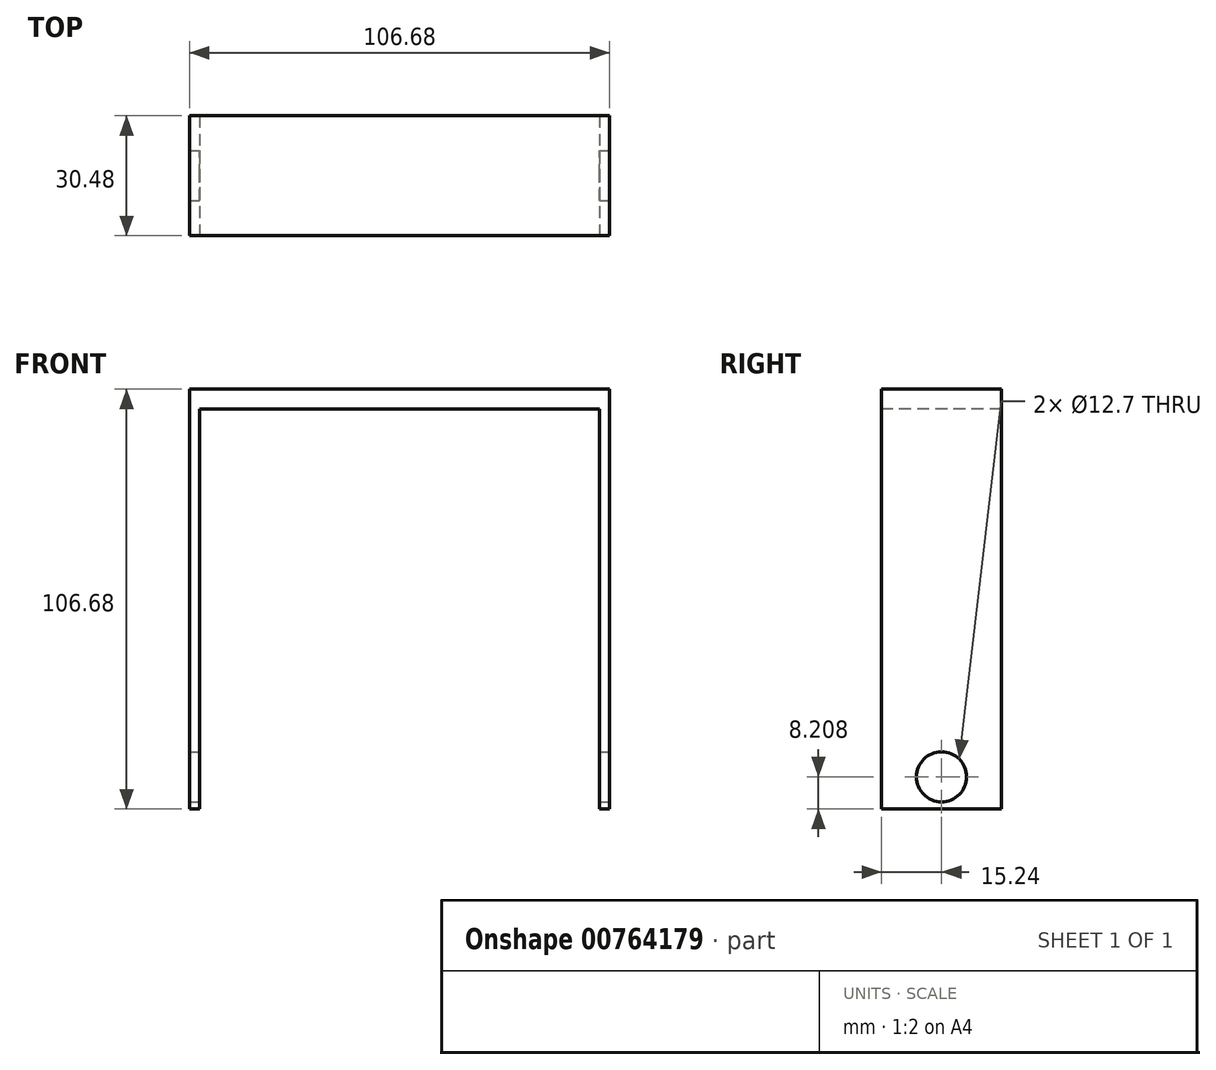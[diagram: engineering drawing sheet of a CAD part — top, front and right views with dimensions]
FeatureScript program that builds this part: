
annotation { "Feature Type Name" : "Feature", "Feature Type Description" : "" }
export const myFeature = defineFeature(function(context is Context, id is Id, definition is map)
    precondition{}
    {
        {
            var Q0;
            Q0=qCreatedBy(makeId("Front.planeOp"),FACE);
            var sketch = newSketch(context, id + "F0", { "sketchPlane" : qUnion([Q0])});
            skLineSegment(sketch, "E0.bottom", {"start": v(0, 0) * mm, "end": v(106.68, 0) * mm});
            skLineSegment(sketch, "E0.top", {"start": v(0, 106.68) * mm, "end": v(106.68, 106.68) * mm});
            skLineSegment(sketch, "E0.left", {"start": v(0, 0) * mm, "end": v(0, 106.68) * mm});
            skLineSegment(sketch, "E0.right", {"start": v(106.68, 0) * mm, "end": v(106.68, 106.68) * mm});
            skSolve(sketch);
        }
        {
            var Q0;
            Q0=makeQuery(id+"F0.imprint","IMPRINT",FACE,{"disambiguationData":[TD([[makeQuery(id+"F0.imprint","IMPRINT",EDGE,{"derivedFrom":sQuery(id+"F0.wireOp",EDGE,"E0.bottom")}),1.0]])]});
            extrude(context, id + "F1", {"entities" : qUnion([Q0]), "depth" : 30.48 * mm, "offsetDistance" : 25.4 * mm});
        }
        {
            var Q0;
            Q0=makeQuery(id+"F1.opExtrude","CAP_FACE",FACE,{"disambiguationData":[OSD([sQuery(id+"F0.wireOp",EDGE,"E0.bottom"),sQuery(id+"F0.wireOp",EDGE,"E0.top"),sQuery(id+"F0.wireOp",EDGE,"E0.left"),sQuery(id+"F0.wireOp",EDGE,"E0.right")])],"isStart":false});
            var sketch = newSketch(context, id + "F2", { "sketchPlane" : qUnion([Q0])});
            skLineSegment(sketch, "E1.bottom", {"start": v(2.54, 0) * mm, "end": v(104.14, 0) * mm});
            skLineSegment(sketch, "E1.top", {"start": v(2.54, 101.6) * mm, "end": v(104.14, 101.6) * mm});
            skLineSegment(sketch, "E1.left", {"start": v(2.54, 0) * mm, "end": v(2.54, 101.6) * mm});
            skLineSegment(sketch, "E1.right", {"start": v(104.14, 0) * mm, "end": v(104.14, 101.6) * mm});
            skSolve(sketch);
        }
        {
            var Q0;
            Q0=makeQuery(id+"F2.imprint","IMPRINT",FACE,{"disambiguationData":[TD([[makeQuery(id+"F2.imprint","IMPRINT",EDGE,{"derivedFrom":sQuery(id+"F2.wireOp",EDGE,"E1.bottom")}),1.0]])]});
            extrude(context, id + "F3", {"entities" : qUnion([Q0]), "operationType" : NewBodyOperationType.REMOVE, "oppositeDirection" : true, "depth" : 30.48 * mm, "offsetDistance" : 25.4 * mm});
        }
        {
            var Q0;
            Q0=makeQuery(id+"F1.opExtrude","SWEPT_FACE",FACE,{"disambiguationData":[OSD([sQuery(id+"F0.wireOp",EDGE,"E0.right")])]});
            var sketch = newSketch(context, id + "F4", { "sketchPlane" : qUnion([Q0])});
            skCircle(sketch, "E2", {"center": v(-15.24, 8.2) * mm, "radius": 6.35 * mm});
            skSolve(sketch);
        }
        {
            var Q0;
            Q0=makeQuery(id+"F4.imprint","IMPRINT",FACE,{"disambiguationData":[TD([[makeQuery(id+"F4.imprint","IMPRINT",EDGE,{"derivedFrom":sQuery(id+"F4.wireOp",EDGE,"E2")}),1.0]])]});
            var Q1;
            Q1=sQuery(id+"F4.wireOp",EDGE,"E2");
            extrude(context, id + "F5", {"entities" : qUnion([Q0]), "operationType" : NewBodyOperationType.REMOVE, "surfaceEntities" : qUnion([Q1]), "oppositeDirection" : true, "depth" : 106.68 * mm, "offsetDistance" : 25.4 * mm});
        }
    });
